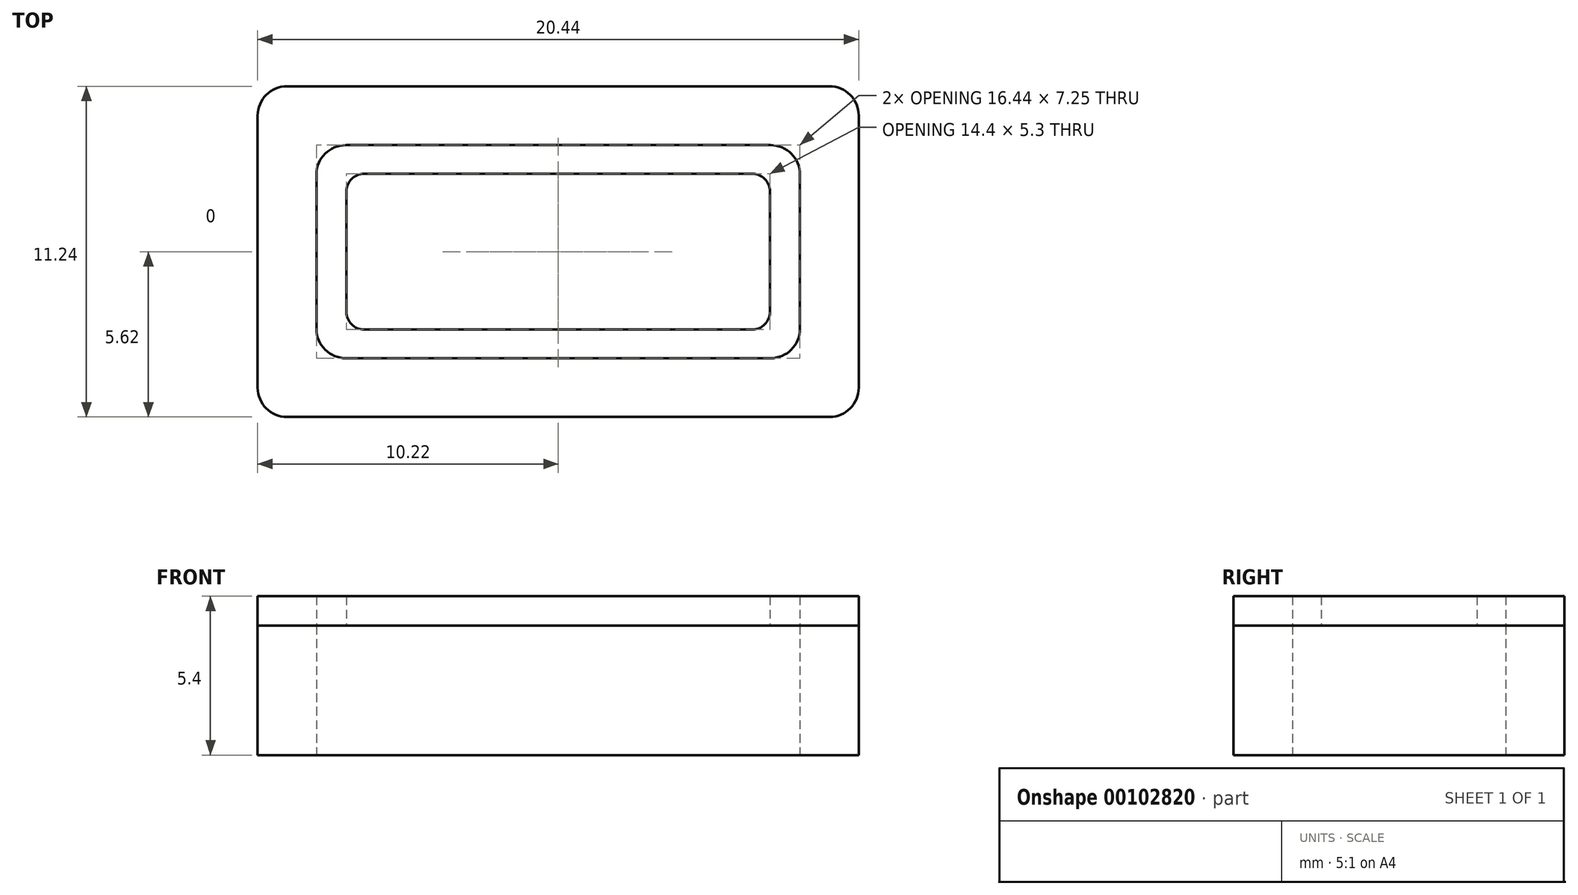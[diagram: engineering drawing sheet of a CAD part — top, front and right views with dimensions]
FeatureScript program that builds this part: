
annotation { "Feature Type Name" : "Feature", "Feature Type Description" : "" }
export const myFeature = defineFeature(function(context is Context, id is Id, definition is map)
    precondition{}
    {
        {
            var Q0;
            Q0=qCreatedBy(makeId("Top.planeOp"),FACE);
            var sketch = newSketch(context, id + "F0", { "sketchPlane" : qUnion([Q0])});
            skLineSegment(sketch, "E0.bottom", {"start": v(8.12, -3.52) * mm, "end": v(-8.12, -3.53) * mm, "construction": true});
            skLineSegment(sketch, "E0.top", {"start": v(8.12, 3.53) * mm, "end": v(-8.12, 3.52) * mm, "construction": true});
            skLineSegment(sketch, "E0.left", {"start": v(8.12, -3.52) * mm, "end": v(8.12, 3.53) * mm, "construction": true});
            skLineSegment(sketch, "E0.right", {"start": v(-8.12, -3.53) * mm, "end": v(-8.12, 3.52) * mm, "construction": true});
            skPoint(sketch, "E0.middle", {"position": v(0, 0) * mm});
            skLineSegment(sketch, "E1.0", {"start": v(7.22, 3.63) * mm, "end": v(-7.22, 3.62) * mm});
            skLineSegment(sketch, "E1.1", {"start": v(8.22, -2.62) * mm, "end": v(8.22, 2.63) * mm});
            skLineSegment(sketch, "E1.2", {"start": v(7.22, -3.62) * mm, "end": v(-7.22, -3.63) * mm});
            skLineSegment(sketch, "E1.3", {"start": v(-8.22, -2.63) * mm, "end": v(-8.22, 2.62) * mm});
            skLineSegment(sketch, "E2.0", {"start": v(9.22, 5.63) * mm, "end": v(-9.22, 5.62) * mm});
            skLineSegment(sketch, "E2.1", {"start": v(10.22, -4.63) * mm, "end": v(10.22, 4.63) * mm});
            skLineSegment(sketch, "E2.2", {"start": v(9.22, -5.62) * mm, "end": v(-9.22, -5.63) * mm});
            skLineSegment(sketch, "E2.3", {"start": v(-10.22, -4.63) * mm, "end": v(-10.22, 4.62) * mm});
            skPoint(sketch, "E3.visualSharp", {"position": v(-8.22, 3.62) * mm});
            skArc(sketch, "E3.filletArc", {"start": v(-7.22, 3.62) * mm, "mid": v(-7.93, 3.33) * mm, "end": v(-8.22, 2.62) * mm});
            skPoint(sketch, "E4.visualSharp", {"position": v(8.22, 3.63) * mm});
            skArc(sketch, "E4.filletArc", {"start": v(8.22, 2.63) * mm, "mid": v(7.93, 3.33) * mm, "end": v(7.22, 3.63) * mm});
            skPoint(sketch, "E5.visualSharp", {"position": v(8.22, -3.62) * mm});
            skArc(sketch, "E5.filletArc", {"start": v(7.22, -3.62) * mm, "mid": v(7.93, -3.33) * mm, "end": v(8.22, -2.62) * mm});
            skPoint(sketch, "E6.visualSharp", {"position": v(-8.22, -3.63) * mm});
            skArc(sketch, "E6.filletArc", {"start": v(-8.22, -2.63) * mm, "mid": v(-7.93, -3.33) * mm, "end": v(-7.22, -3.63) * mm});
            skPoint(sketch, "E7.visualSharp", {"position": v(-10.22, -5.63) * mm});
            skArc(sketch, "E7.filletArc", {"start": v(-10.22, -4.63) * mm, "mid": v(-9.93, -5.33) * mm, "end": v(-9.22, -5.63) * mm});
            skPoint(sketch, "E8.visualSharp", {"position": v(-10.22, 5.62) * mm});
            skArc(sketch, "E8.filletArc", {"start": v(-9.22, 5.62) * mm, "mid": v(-9.93, 5.33) * mm, "end": v(-10.22, 4.62) * mm});
            skPoint(sketch, "E9.visualSharp", {"position": v(10.22, 5.63) * mm});
            skArc(sketch, "E9.filletArc", {"start": v(10.22, 4.63) * mm, "mid": v(9.93, 5.33) * mm, "end": v(9.22, 5.63) * mm});
            skPoint(sketch, "E10.visualSharp", {"position": v(10.22, -5.62) * mm});
            skArc(sketch, "E10.filletArc", {"start": v(9.22, -5.62) * mm, "mid": v(9.93, -5.33) * mm, "end": v(10.22, -4.63) * mm});
            skSolve(sketch);
        }
        {
            var Q0;
            Q0=makeQuery(id+"F0.imprint","IMPRINT",FACE,{"disambiguationData":[TD([[makeQuery(id+"F0.imprint","IMPRINT",EDGE,{"derivedFrom":sQuery(id+"F0.wireOp",EDGE,"E1.0")}),-1.0]])]});
            extrude(context, id + "F1", {"entities" : qUnion([Q0]), "depth" : 4.4 * mm});
        }
        {
            var Q0;
            Q0=makeQuery(id+"F1.opExtrude","CAP_FACE",FACE,{"disambiguationData":[OSD([sQuery(id+"F0.wireOp",EDGE,"E1.0"),sQuery(id+"F0.wireOp",EDGE,"E1.1"),sQuery(id+"F0.wireOp",EDGE,"E1.2"),sQuery(id+"F0.wireOp",EDGE,"E1.3"),sQuery(id+"F0.wireOp",EDGE,"E2.0"),sQuery(id+"F0.wireOp",EDGE,"E2.1"),sQuery(id+"F0.wireOp",EDGE,"E2.2"),sQuery(id+"F0.wireOp",EDGE,"E2.3"),sQuery(id+"F0.wireOp",EDGE,"E3.filletArc"),sQuery(id+"F0.wireOp",EDGE,"E4.filletArc"),sQuery(id+"F0.wireOp",EDGE,"E5.filletArc"),sQuery(id+"F0.wireOp",EDGE,"E6.filletArc"),sQuery(id+"F0.wireOp",EDGE,"E7.filletArc"),sQuery(id+"F0.wireOp",EDGE,"E8.filletArc"),sQuery(id+"F0.wireOp",EDGE,"E9.filletArc"),sQuery(id+"F0.wireOp",EDGE,"E10.filletArc")])],"isStart":false});
            var sketch = newSketch(context, id + "F2", { "sketchPlane" : qUnion([Q0])});
            skArc(sketch, "E11", {"start": v(10.22, 4.63) * mm, "mid": v(9.93, 5.33) * mm, "end": v(9.22, 5.63) * mm});
            skLineSegment(sketch, "E12", {"start": v(10.22, -4.63) * mm, "end": v(10.22, 4.63) * mm});
            skArc(sketch, "E13", {"start": v(9.22, -5.62) * mm, "mid": v(9.93, -5.33) * mm, "end": v(10.22, -4.63) * mm});
            skLineSegment(sketch, "E14", {"start": v(9.22, -5.62) * mm, "end": v(-9.22, -5.63) * mm});
            skArc(sketch, "E15", {"start": v(-10.22, -4.63) * mm, "mid": v(-9.93, -5.33) * mm, "end": v(-9.22, -5.63) * mm});
            skLineSegment(sketch, "E16", {"start": v(-10.22, -4.63) * mm, "end": v(-10.22, 4.62) * mm});
            skArc(sketch, "E17", {"start": v(-9.22, 5.62) * mm, "mid": v(-9.93, 5.33) * mm, "end": v(-10.22, 4.62) * mm});
            skLineSegment(sketch, "E18", {"start": v(9.22, 5.63) * mm, "end": v(-9.22, 5.62) * mm});
            skArc(sketch, "E19", {"start": v(-7.22, 3.62) * mm, "mid": v(-7.93, 3.33) * mm, "end": v(-8.22, 2.62) * mm});
            skLineSegment(sketch, "E20", {"start": v(-8.22, -2.63) * mm, "end": v(-8.22, 2.62) * mm});
            skArc(sketch, "E21", {"start": v(-8.22, -2.63) * mm, "mid": v(-7.93, -3.33) * mm, "end": v(-7.22, -3.63) * mm});
            skLineSegment(sketch, "E22", {"start": v(7.22, -3.62) * mm, "end": v(-7.22, -3.63) * mm});
            skArc(sketch, "E23", {"start": v(7.22, -3.62) * mm, "mid": v(7.93, -3.33) * mm, "end": v(8.22, -2.62) * mm});
            skLineSegment(sketch, "E24", {"start": v(8.22, -2.62) * mm, "end": v(8.22, 2.63) * mm});
            skArc(sketch, "E25", {"start": v(8.22, 2.63) * mm, "mid": v(7.93, 3.33) * mm, "end": v(7.22, 3.63) * mm});
            skLineSegment(sketch, "E26", {"start": v(7.22, 3.63) * mm, "end": v(-7.22, 3.62) * mm});
            skPoint(sketch, "E27.middle", {"position": v(-0.16, 0) * mm});
            skPoint(sketch, "E27.top.end.orphan", {"position": v(-7.26, 1.64) * mm});
            skPoint(sketch, "E27.bottom.end.orphan", {"position": v(-7.26, -1.64) * mm});
            skPoint(sketch, "E27.left.end.orphan", {"position": v(6.94, 1.64) * mm});
            skPoint(sketch, "E27.left.start.orphan", {"position": v(6.94, -1.64) * mm});
            skLineSegment(sketch, "E28.bottom", {"start": v(6.6, -2.65) * mm, "end": v(-6.6, -2.65) * mm});
            skLineSegment(sketch, "E28.top", {"start": v(6.6, 2.65) * mm, "end": v(-6.6, 2.65) * mm});
            skLineSegment(sketch, "E28.left", {"start": v(7.2, -2.05) * mm, "end": v(7.2, 2.05) * mm});
            skLineSegment(sketch, "E28.right", {"start": v(-7.2, -2.05) * mm, "end": v(-7.2, 2.05) * mm});
            skPoint(sketch, "E28.middle", {"position": v(0, 0) * mm});
            skPoint(sketch, "E29", {"position": v(0, -2.65) * mm});
            skPoint(sketch, "E30", {"position": v(-4.1, -2.65) * mm});
            skPoint(sketch, "E31", {"position": v(4.1, -2.65) * mm});
            skLineSegment(sketch, "E32", {"start": v(-4.1, -2.65) * mm, "end": v(-4.1, -3.63) * mm, "construction": true});
            skLineSegment(sketch, "E33", {"start": v(4.1, -2.65) * mm, "end": v(4.1, -3.62) * mm, "construction": true});
            skPoint(sketch, "E34.visualSharp", {"position": v(-7.2, 2.65) * mm});
            skArc(sketch, "E34.filletArc", {"start": v(-6.6, 2.65) * mm, "mid": v(-7.02, 2.47) * mm, "end": v(-7.2, 2.05) * mm});
            skPoint(sketch, "E35.visualSharp", {"position": v(7.2, 2.65) * mm});
            skArc(sketch, "E35.filletArc", {"start": v(7.2, 2.05) * mm, "mid": v(7.02, 2.47) * mm, "end": v(6.6, 2.65) * mm});
            skPoint(sketch, "E36.visualSharp", {"position": v(7.2, -2.65) * mm});
            skArc(sketch, "E36.filletArc", {"start": v(6.6, -2.65) * mm, "mid": v(7.02, -2.47) * mm, "end": v(7.2, -2.05) * mm});
            skPoint(sketch, "E37.visualSharp", {"position": v(-7.2, -2.65) * mm});
            skArc(sketch, "E37.filletArc", {"start": v(-7.2, -2.05) * mm, "mid": v(-7.02, -2.47) * mm, "end": v(-6.6, -2.65) * mm});
            skSolve(sketch);
        }
        {
            var Q0;
            Q0=makeQuery(id+"F2.imprint","IMPRINT",FACE,{"disambiguationData":[TD([[makeQuery(id+"F2.imprint","IMPRINT",EDGE,{"derivedFrom":sQuery(id+"F2.wireOp",EDGE,"E19")}),1.0]])]});
            extrude(context, id + "F3", {"entities" : qUnion([Q0]), "depth" : 1 * mm});
        }
        {
            var Q0;
            Q0=makeQuery(id+"F1.opExtrude","CAP_FACE",FACE,{"disambiguationData":[OSD([sQuery(id+"F0.wireOp",EDGE,"E1.0"),sQuery(id+"F0.wireOp",EDGE,"E1.1"),sQuery(id+"F0.wireOp",EDGE,"E1.2"),sQuery(id+"F0.wireOp",EDGE,"E1.3"),sQuery(id+"F0.wireOp",EDGE,"E2.0"),sQuery(id+"F0.wireOp",EDGE,"E2.1"),sQuery(id+"F0.wireOp",EDGE,"E2.2"),sQuery(id+"F0.wireOp",EDGE,"E2.3"),sQuery(id+"F0.wireOp",EDGE,"E3.filletArc"),sQuery(id+"F0.wireOp",EDGE,"E4.filletArc"),sQuery(id+"F0.wireOp",EDGE,"E5.filletArc"),sQuery(id+"F0.wireOp",EDGE,"E6.filletArc"),sQuery(id+"F0.wireOp",EDGE,"E7.filletArc"),sQuery(id+"F0.wireOp",EDGE,"E8.filletArc"),sQuery(id+"F0.wireOp",EDGE,"E9.filletArc"),sQuery(id+"F0.wireOp",EDGE,"E10.filletArc")])],"isStart":false});
            extrude(context, id + "F4", {"entities" : qUnion([Q0]), "depth" : 1 * mm});
        }
    });
